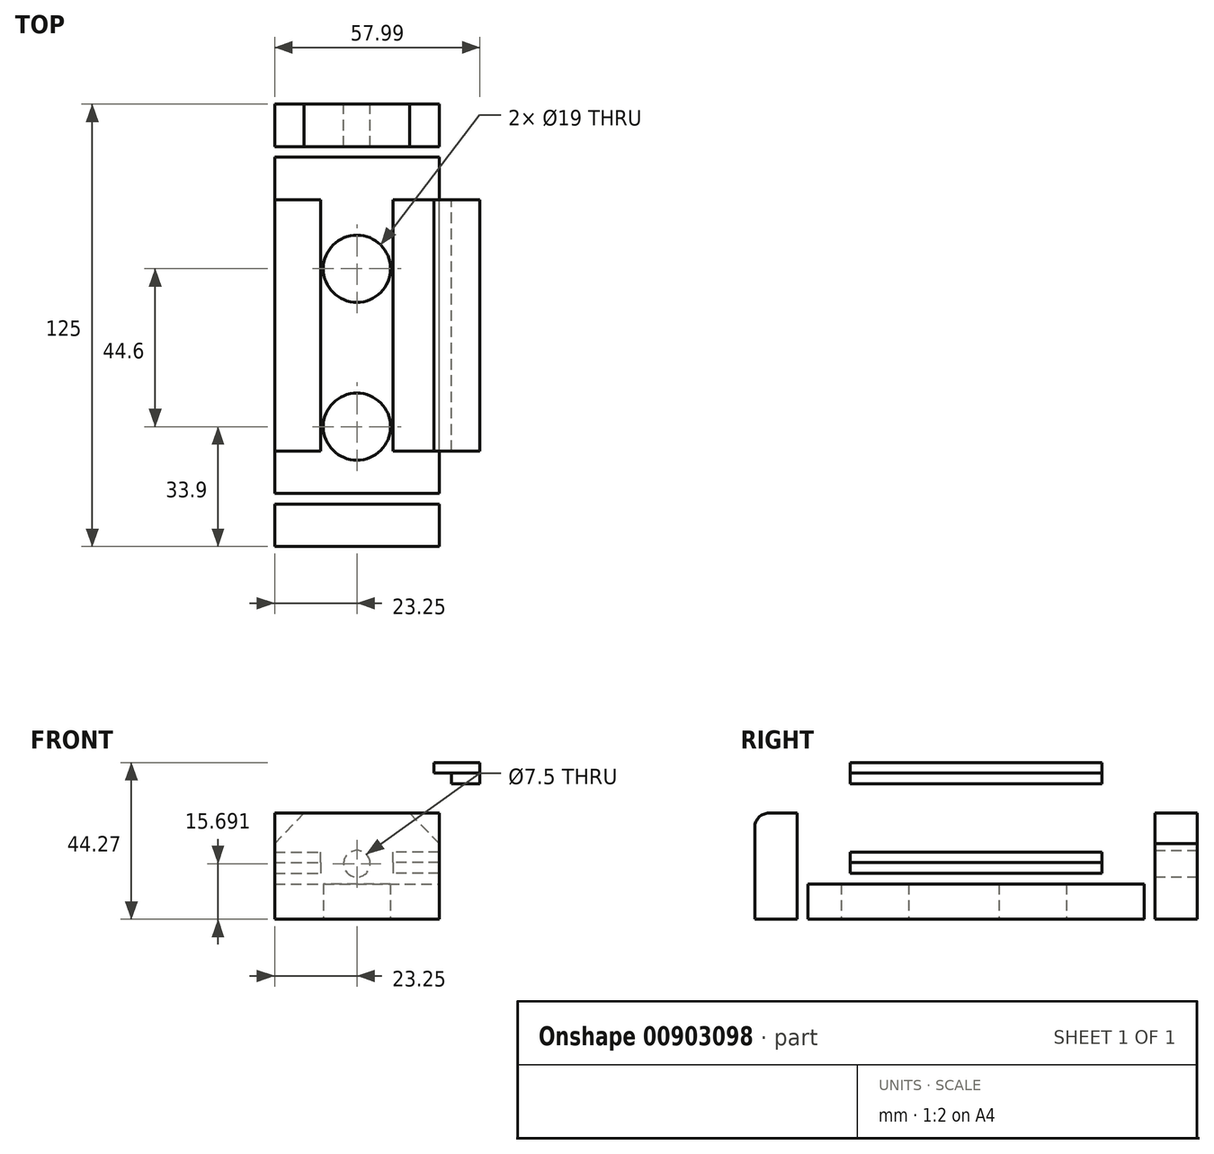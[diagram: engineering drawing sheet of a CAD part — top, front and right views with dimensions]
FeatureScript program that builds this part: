
annotation { "Feature Type Name" : "Feature", "Feature Type Description" : "" }
export const myFeature = defineFeature(function(context is Context, id is Id, definition is map)
    precondition{}
    {
        {
            var Q0;
            Q0=qCreatedBy(makeId("Front.planeOp"),FACE);
            var sketch = newSketch(context, id + "F0", { "sketchPlane" : qUnion([Q0])});
            skLineSegment(sketch, "E0.bottom", {"start": v(0, 0) * mm, "end": v(46.5, 0) * mm});
            skLineSegment(sketch, "E0.top", {"start": v(8.34, 30) * mm, "end": v(38.16, 30) * mm});
            skLineSegment(sketch, "E0.left", {"start": v(0, 0) * mm, "end": v(0, 21.37) * mm});
            skLineSegment(sketch, "E0.right", {"start": v(46.5, 0) * mm, "end": v(46.5, 21.37) * mm});
            skLineSegment(sketch, "E1", {"start": v(8.34, 30) * mm, "end": v(0, 21.37) * mm});
            skLineSegment(sketch, "E2", {"start": v(4.17, 25.68) * mm, "end": v(-10.32, 39.68) * mm, "construction": true});
            skLineSegment(sketch, "E3", {"start": v(23.25, 30) * mm, "end": v(23.25, 51.58) * mm});
            skLineSegment(sketch, "E4", {"start": v(23.25, 51.58) * mm, "end": v(23.25, -20.2) * mm, "construction": true});
            skPoint(sketch, "E4.endSnap0", {"position": v(23.25, 0) * mm});
            skLineSegment(sketch, "E5.MirrorCS", {"start": v(38.16, 30) * mm, "end": v(8.34, 30) * mm});
            skLineSegment(sketch, "E6.MirrorCS", {"start": v(38.16, 30) * mm, "end": v(46.5, 21.37) * mm});
            skLineSegment(sketch, "E7.MirrorCS", {"start": v(46.5, 0) * mm, "end": v(0, 0) * mm});
            skPoint(sketch, "E8.orphan", {"position": v(0, 30) * mm});
            skLineSegment(sketch, "E9.trimOffspring", {"start": v(0, 29.7) * mm, "end": v(0, 30) * mm});
            skPoint(sketch, "E10.orphan", {"position": v(46.5, 30) * mm});
            skCircle(sketch, "E11", {"center": v(23.25, 15.7) * mm, "radius": 3.75 * mm});
            skSolve(sketch);
        }
        {
            var Q0;
            Q0 = qSketchRegion(id + "F0", true);
            extrude(context, id + "F1", {"entities" : qUnion([Q0]), "depth" : 12 * mm, "offsetDistance" : 25 * mm});
        }
        {
            var Q0;
            Q0=qCreatedBy(makeId("Front.planeOp"),FACE);
            cPlane(context, id + "F2", {"entities" : qUnion([Q0]), "cplaneType" : CPlaneType.OFFSET, "offset" : 15 * mm, "width" : 150 * mm, "height" : 150 * mm});
        }
        {
            var Q0;
            Q0=qCreatedBy(id+"F2.planeOp",FACE);
            var sketch = newSketch(context, id + "F3", { "sketchPlane" : qUnion([Q0])});
            skLineSegment(sketch, "E12.bottom", {"start": v(0, 0) * mm, "end": v(46.5, 0) * mm});
            skLineSegment(sketch, "E12.top", {"start": v(0, 10) * mm, "end": v(46.5, 10) * mm});
            skLineSegment(sketch, "E12.left", {"start": v(0, 0) * mm, "end": v(0, 10) * mm});
            skLineSegment(sketch, "E12.right", {"start": v(46.5, 0) * mm, "end": v(46.5, 10) * mm});
            skSolve(sketch);
        }
        {
            var Q0;
            Q0 = qSketchRegion(id + "F3", true);
            extrude(context, id + "F4", {"entities" : qUnion([Q0]), "depth" : 95 * mm, "offsetDistance" : 25 * mm});
        }
        {
            var Q0;
            Q0=qCreatedBy(makeId("Front.planeOp"),FACE);
            cPlane(context, id + "F5", {"entities" : qUnion([Q0]), "cplaneType" : CPlaneType.OFFSET, "offset" : 113 * mm, "width" : 150 * mm, "height" : 150 * mm});
        }
        {
            var Q0;
            Q0=qCreatedBy(id+"F5.planeOp",FACE);
            var sketch = newSketch(context, id + "F6", { "sketchPlane" : qUnion([Q0])});
            skLineSegment(sketch, "E13.bottom", {"start": v(0, 0) * mm, "end": v(46.5, 0) * mm});
            skLineSegment(sketch, "E13.top", {"start": v(0, 30) * mm, "end": v(46.5, 30) * mm});
            skLineSegment(sketch, "E13.left", {"start": v(0, 0) * mm, "end": v(0, 30) * mm});
            skLineSegment(sketch, "E13.right", {"start": v(46.5, 0) * mm, "end": v(46.5, 30) * mm});
            skSolve(sketch);
        }
        {
            var Q0;
            Q0 = qSketchRegion(id + "F6", true);
            extrude(context, id + "F7", {"entities" : qUnion([Q0]), "depth" : 12 * mm, "offsetDistance" : 25 * mm});
        }
        {
            var Q0;
            Q0=makeQuery(id+"F7.opExtrude","CAP_EDGE",EDGE,{"disambiguationData":[OSD([sQuery(id+"F6.wireOp",EDGE,"E13.top")])],"isStart":false});
            fillet(context, id + "F8", {"entities" : qUnion([Q0]), "radius" : 4 * mm, "tangentPropagation" : true, "allowEdgeOverflow" : false});
        }
        {
            var Q0;
            Q0=qCreatedBy(makeId("Top.planeOp"),FACE);
            cPlane(context, id + "F9", {"entities" : qUnion([Q0]), "cplaneType" : CPlaneType.OFFSET, "offset" : 13 * mm, "width" : 150 * mm, "height" : 150 * mm});
        }
        {
            var Q0;
            Q0=qCreatedBy(id+"F9.planeOp",FACE);
            var sketch = newSketch(context, id + "F10", { "sketchPlane" : qUnion([Q0])});
            skLineSegment(sketch, "E14.bottom", {"start": v(46.5, -27) * mm, "end": v(33.5, -27) * mm});
            skLineSegment(sketch, "E14.top", {"start": v(46.5, -98) * mm, "end": v(33.5, -98) * mm});
            skLineSegment(sketch, "E14.left", {"start": v(46.5, -27) * mm, "end": v(46.5, -98) * mm});
            skLineSegment(sketch, "E14.right", {"start": v(33.5, -27) * mm, "end": v(33.5, -98) * mm});
            skLineSegment(sketch, "E15", {"start": v(46.53, -102.9) * mm, "end": v(0, -102.9) * mm, "construction": true});
            skLineSegment(sketch, "E16", {"start": v(23.27, -102.9) * mm, "end": v(23.27, -18.63) * mm, "construction": true});
            skLineSegment(sketch, "E17.MirrorCS", {"start": v(13.03, -27) * mm, "end": v(13.03, -98) * mm});
            skLineSegment(sketch, "E18.MirrorCS", {"start": v(0.03, -27) * mm, "end": v(13.03, -27) * mm});
            skLineSegment(sketch, "E19.MirrorCS", {"start": v(0.03, -27) * mm, "end": v(0.03, -98) * mm});
            skLineSegment(sketch, "E20.MirrorCS", {"start": v(0.03, -98) * mm, "end": v(13.03, -98) * mm});
            skSolve(sketch);
        }
        {
            var Q0;
            Q0 = qSketchRegion(id + "F10", true);
            extrude(context, id + "F11", {"entities" : qUnion([Q0]), "depth" : 3 * mm, "offsetDistance" : 25 * mm});
        }
        {
            var Q0;
            Q0=qCreatedBy(id+"F9.planeOp",FACE);
            cPlane(context, id + "F12", {"entities" : qUnion([Q0]), "cplaneType" : CPlaneType.OFFSET, "offset" : 3 * mm, "width" : 150 * mm, "height" : 150 * mm});
        }
        {
            var Q0;
            Q0=makeQuery(id+"F11.opExtrude","SWEPT_BODY",BODY,{"disambiguationData":[OSD([sQuery(id+"F10.wireOp",EDGE,"E14.bottom"),sQuery(id+"F10.wireOp",EDGE,"E14.top"),sQuery(id+"F10.wireOp",EDGE,"E14.left"),sQuery(id+"F10.wireOp",EDGE,"E14.right")])]});
            var Q1;
            Q1=makeQuery(id+"F11.opExtrude","SWEPT_BODY",BODY,{"disambiguationData":[OSD([sQuery(id+"F10.wireOp",EDGE,"E17.MirrorCS"),sQuery(id+"F10.wireOp",EDGE,"E18.MirrorCS"),sQuery(id+"F10.wireOp",EDGE,"E19.MirrorCS"),sQuery(id+"F10.wireOp",EDGE,"E20.MirrorCS")])]});
            var Q2;
            Q2=qCreatedBy(id+"F12.planeOp",FACE);
            mirror(context, id + "F13", {"entities" : qUnion([Q0, Q1]), "mirrorPlane" : qUnion([Q2])});
        }
        {
            var Q0;
            Q0=makeQuery(id+"F4.opExtrude","SWEPT_FACE",FACE,{"disambiguationData":[OSD([sQuery(id+"F3.wireOp",EDGE,"E12.bottom")])]});
            var sketch = newSketch(context, id + "F14", { "sketchPlane" : qUnion([Q0])});
            skLineSegment(sketch, "E21", {"start": v(23.25, 110) * mm, "end": v(23.25, 15) * mm, "construction": true});
            skCircle(sketch, "E22", {"center": v(23.25, 91.1) * mm, "radius": 9.5 * mm});
            skCircle(sketch, "E23", {"center": v(23.25, 46.5) * mm, "radius": 9.5 * mm});
            skSolve(sketch);
        }
        {
            var Q0;
            Q0 = qSketchRegion(id + "F14", true);
            var Q1;
            Q1=makeQuery(id+"F4.opExtrude","SWEPT_FACE",FACE,{"disambiguationData":[OSD([sQuery(id+"F3.wireOp",EDGE,"E12.top")])]});
            extrude(context, id + "F15", {"entities" : qUnion([Q0]), "operationType" : NewBodyOperationType.REMOVE, "endBound" : BoundingType.UP_TO_NEXT, "oppositeDirection" : true, "depth" : 10 * mm, "endBoundEntityFace" : qUnion([Q1]), "offsetDistance" : 25 * mm});
        }
        {
            var Q0;
            Q0=makeQuery(id+"F4.opExtrude","CAP_FACE",FACE,{"disambiguationData":[OSD([sQuery(id+"F3.wireOp",EDGE,"E12.bottom"),sQuery(id+"F3.wireOp",EDGE,"E12.top"),sQuery(id+"F3.wireOp",EDGE,"E12.left"),sQuery(id+"F3.wireOp",EDGE,"E12.right")])],"isStart":true});
            cPlane(context, id + "F16", {"entities" : qUnion([Q0]), "cplaneType" : CPlaneType.OFFSET, "offset" : 12 * mm, "oppositeDirection" : true, "width" : 150 * mm, "height" : 150 * mm});
        }
        {
            var Q0;
            Q0=qCreatedBy(id+"F16.planeOp",FACE);
            var sketch = newSketch(context, id + "F17", { "sketchPlane" : qUnion([Q0])});
            skLineSegment(sketch, "E24.bottom", {"start": v(-45, 44.27) * mm, "end": v(-58, 44.27) * mm});
            skLineSegment(sketch, "E24.top", {"start": v(-50, 38.27) * mm, "end": v(-58, 38.27) * mm});
            skLineSegment(sketch, "E24.left", {"start": v(-45, 44.27) * mm, "end": v(-45, 41.27) * mm});
            skLineSegment(sketch, "E24.right", {"start": v(-58, 44.27) * mm, "end": v(-58, 38.27) * mm});
            skLineSegment(sketch, "E25.bottom", {"start": v(-58, 41.27) * mm, "end": v(-45, 41.27) * mm});
            skLineSegment(sketch, "E25.top", {"start": v(-58, 41.27) * mm, "end": v(-45, 41.27) * mm});
            skLineSegment(sketch, "E25.left", {"start": v(-58, 41.27) * mm, "end": v(-58, 41.27) * mm});
            skLineSegment(sketch, "E25.right", {"start": v(-45, 41.27) * mm, "end": v(-45, 41.27) * mm});
            skLineSegment(sketch, "E26.bottom", {"start": v(-53.36, 41.27) * mm, "end": v(-50, 41.27) * mm});
            skLineSegment(sketch, "E26.top", {"start": v(-53.36, 38.27) * mm, "end": v(-50, 38.27) * mm});
            skLineSegment(sketch, "E26.right", {"start": v(-50, 41.27) * mm, "end": v(-50, 38.27) * mm});
            skPoint(sketch, "E27.orphan", {"position": v(-45, 38.27) * mm});
            skSolve(sketch);
        }
        {
            var Q0;
            {var subQ4=sQuery(id+"F17.wireOp",EDGE,"E24.top");Q0=makeQuery(id+"F17.imprint","IMPRINT",FACE,{"disambiguationData":[TD([[makeQuery(id+"F17.imprint","IMPRINT",EDGE,{"derivedFrom":subQ4}),-1.0]])]});}
            extrude(context, id + "F18", {"entities" : qUnion([Q0]), "oppositeDirection" : true, "depth" : 71 * mm, "offsetDistance" : 25 * mm});
        }
        {
            var Q0;
            {var subQ1=sQuery(id+"F17.wireOp",EDGE,"E24.bottom");Q0=makeQuery(id+"F17.imprint","IMPRINT",FACE,{"disambiguationData":[TD([[makeQuery(id+"F17.imprint","IMPRINT",EDGE,{"derivedFrom":subQ1}),1.0]])]});}
            extrude(context, id + "F19", {"entities" : qUnion([Q0]), "oppositeDirection" : true, "depth" : 71 * mm, "offsetDistance" : 25 * mm});
        }
    });
